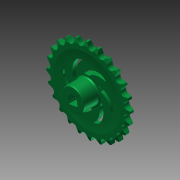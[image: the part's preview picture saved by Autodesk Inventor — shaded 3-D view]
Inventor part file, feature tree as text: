
AUTODESK INVENTOR PART (.ipt)
format: ipt  version: 2012 (Build 160160000, 160)  size: 1,112,064 bytes
history: native  units: in
note: dims shown in document units (in); Inventor stores cm internally (conversion verified against a paired STEP export)
features: other x1, imported_body x1, plane x1
ambient origin geometry x8: Origin, YZ Plane, XZ Plane, XY Plane, X Axis, Y Axis, Z Axis, Center Point
feature tree (3):
  parser-record x1  (decoder bookkeeping rows leaked as tree rows — omitted from the tree; the rows remain in map.json)
  imported_body  "Base1"
  plane  "Work Plane1"
